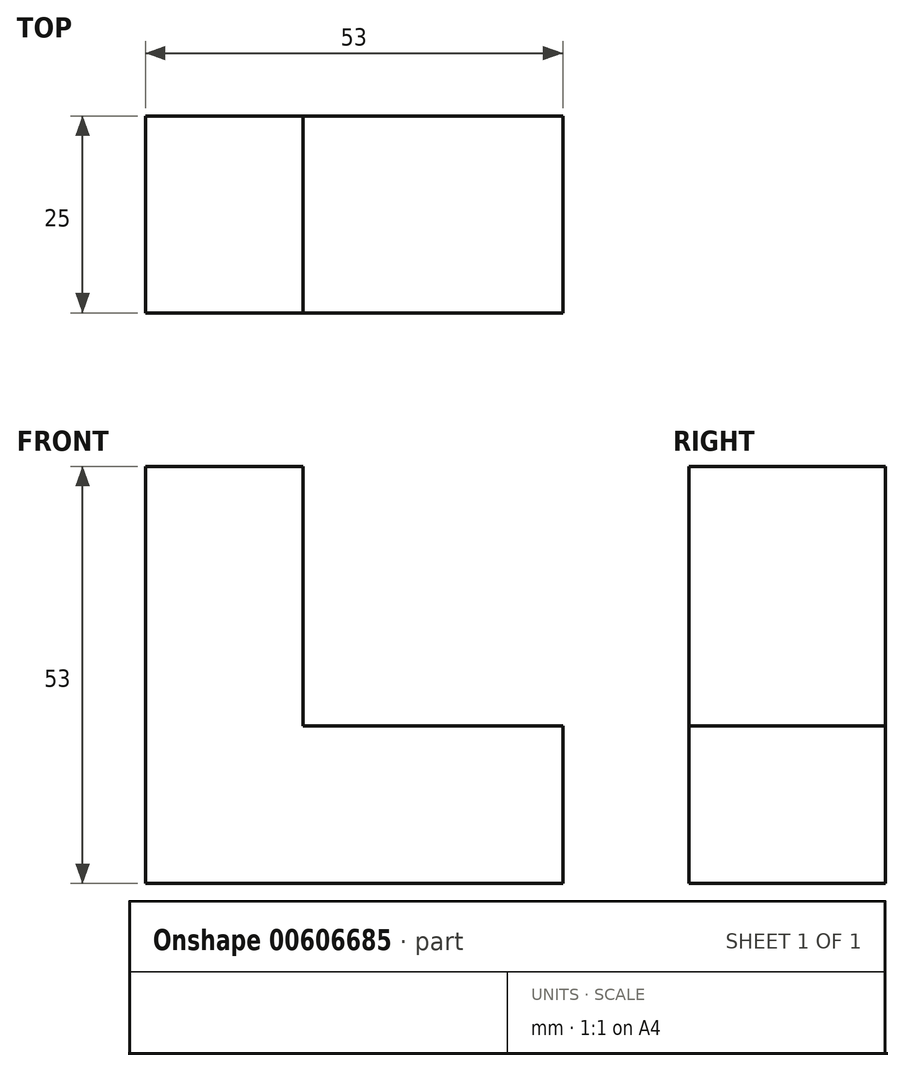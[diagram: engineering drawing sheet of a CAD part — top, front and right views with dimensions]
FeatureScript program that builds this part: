
annotation { "Feature Type Name" : "Feature", "Feature Type Description" : "" }
export const myFeature = defineFeature(function(context is Context, id is Id, definition is map)
    precondition{}
    {
        {
            var Q0;
            Q0=qCreatedBy(makeId("Front.planeOp"),FACE);
            var sketch = newSketch(context, id + "F0", { "sketchPlane" : qUnion([Q0])});
            skLineSegment(sketch, "E0", {"start": v(-40.94, 39.4) * mm, "end": v(-40.94, -13.6) * mm});
            skLineSegment(sketch, "E1", {"start": v(-40.94, -13.6) * mm, "end": v(12.06, -13.6) * mm});
            skLineSegment(sketch, "E2", {"start": v(12.06, -13.6) * mm, "end": v(12.06, 6.4) * mm});
            skLineSegment(sketch, "E3", {"start": v(12.06, 6.4) * mm, "end": v(-20.94, 6.4) * mm});
            skLineSegment(sketch, "E4", {"start": v(-20.94, 6.4) * mm, "end": v(-20.94, 39.4) * mm});
            skLineSegment(sketch, "E5", {"start": v(-20.94, 39.4) * mm, "end": v(-40.94, 39.4) * mm});
            skSolve(sketch);
        }
        {
            var Q0;
            Q0=makeQuery(id+"F0.imprint","IMPRINT",FACE,{"disambiguationData":[TD([[makeQuery(id+"F0.imprint","IMPRINT",EDGE,{"derivedFrom":sQuery(id+"F0.wireOp",EDGE,"E0")}),1.0]])]});
            extrude(context, id + "F1", {"entities" : qUnion([Q0]), "depth" : 25 * mm, "offsetDistance" : 25 * mm});
        }
    });
